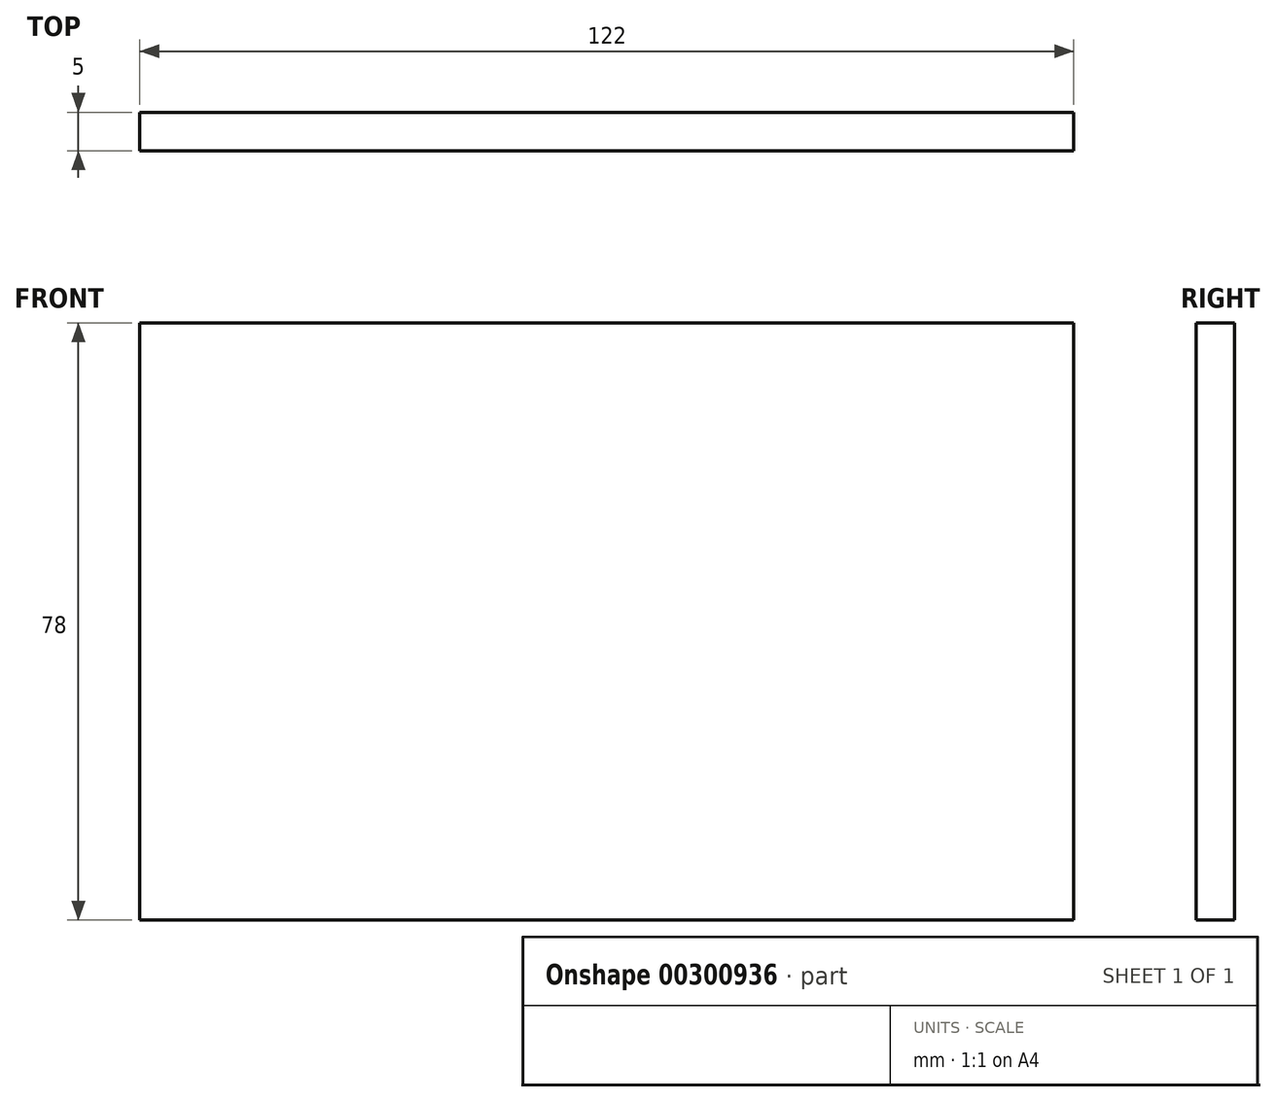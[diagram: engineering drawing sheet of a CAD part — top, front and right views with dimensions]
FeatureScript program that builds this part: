
annotation { "Feature Type Name" : "Feature", "Feature Type Description" : "" }
export const myFeature = defineFeature(function(context is Context, id is Id, definition is map)
    precondition{}
    {
        {
            var Q0;
            Q0=qCreatedBy(makeId("Front.planeOp"),FACE);
            var sketch = newSketch(context, id + "F0", { "sketchPlane" : qUnion([Q0])});
            skLineSegment(sketch, "E0.bottom", {"start": v(0, 0) * mm, "end": v(122, 0) * mm});
            skLineSegment(sketch, "E0.top", {"start": v(0, -78) * mm, "end": v(122, -78) * mm});
            skLineSegment(sketch, "E0.left", {"start": v(0, 0) * mm, "end": v(0, -78) * mm});
            skLineSegment(sketch, "E0.right", {"start": v(122, 0) * mm, "end": v(122, -78) * mm});
            skSolve(sketch);
        }
        {
            var Q0;
            Q0=makeQuery(id+"F0.imprint","IMPRINT",FACE,{"disambiguationData":[TD([[makeQuery(id+"F0.imprint","IMPRINT",EDGE,{"derivedFrom":sQuery(id+"F0.wireOp",EDGE,"E0.bottom")}),-1.0]])]});
            extrude(context, id + "F1", {"entities" : qUnion([Q0]), "depth" : 5 * mm});
        }
        {
            var Q0;
            Q0=makeQuery(id+"F1.opExtrude","SWEPT_BODY",BODY,{"disambiguationData":[OSD([sQuery(id+"F0.wireOp",EDGE,"E0.bottom"),sQuery(id+"F0.wireOp",EDGE,"E0.top"),sQuery(id+"F0.wireOp",EDGE,"E0.left"),sQuery(id+"F0.wireOp",EDGE,"E0.right")])]});
            var Q1;
            Q1=qCreatedBy(makeId("Origin.pointOp"),VERTEX);
            var Q2;
            Q2=qCreatedBy(makeId("Origin.pointOp"),VERTEX);
            transform(context, id + "F2", {"entities" : qUnion([Q0]), "transformType" : TransformType.SCALE_UNIFORMLY, "scale" : 1, "scalePoint" : qUnion([Q2]), "makeCopy" : false});
        }
    });
